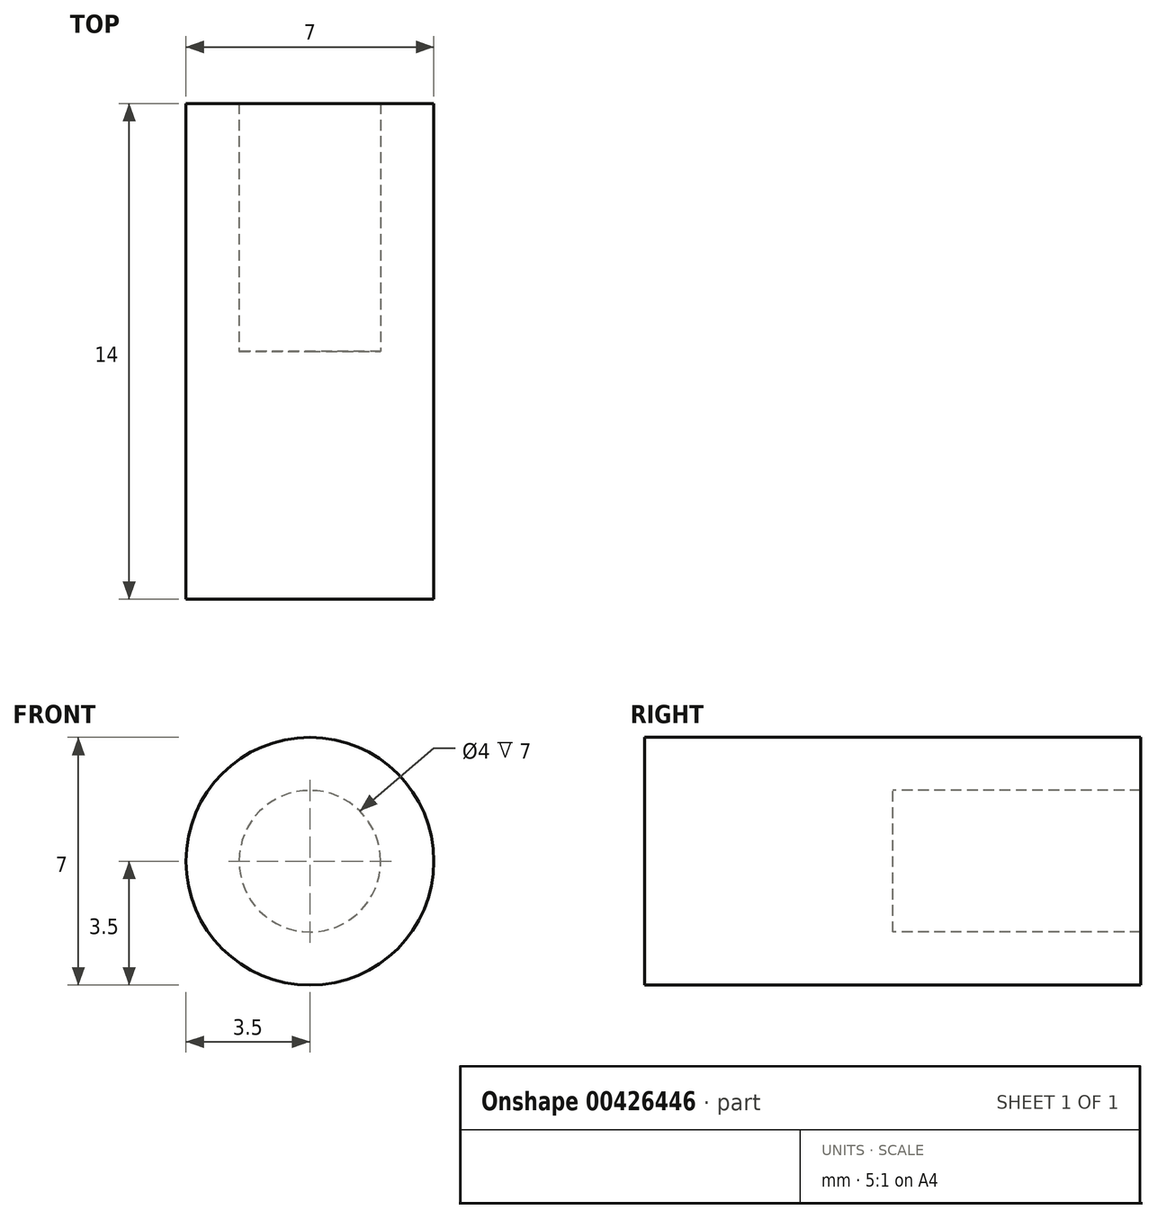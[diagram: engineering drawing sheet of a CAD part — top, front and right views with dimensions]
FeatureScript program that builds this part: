
annotation { "Feature Type Name" : "Feature", "Feature Type Description" : "" }
export const myFeature = defineFeature(function(context is Context, id is Id, definition is map)
    precondition{}
    {
        {
            var Q0;
            Q0=qCreatedBy(makeId("Right.planeOp"),FACE);
            var sketch = newSketch(context, id + "F0", { "sketchPlane" : qUnion([Q0])});
            skLineSegment(sketch, "E0.bottom", {"start": v(-7, 3.5) * mm, "end": v(7, 3.5) * mm});
            skLineSegment(sketch, "E0.left", {"start": v(-7, 3.5) * mm, "end": v(-7, 0) * mm});
            skLineSegment(sketch, "E0.right", {"start": v(7, 3.5) * mm, "end": v(7, 0) * mm});
            skPoint(sketch, "E0.middle", {"position": v(0, 0) * mm});
            skLineSegment(sketch, "E1", {"start": v(-7, 0) * mm, "end": v(0, 0) * mm});
            skLineSegment(sketch, "E2", {"start": v(0, 2) * mm, "end": v(7, 2) * mm});
            skLineSegment(sketch, "E3", {"start": v(0, 0) * mm, "end": v(0, 2) * mm});
            skPoint(sketch, "E4.orphan", {"position": v(-7, 2) * mm});
            skPoint(sketch, "E5.orphan", {"position": v(7, 0) * mm});
            skPoint(sketch, "E6.orphan", {"position": v(7, -3.5) * mm});
            skPoint(sketch, "E7.orphan", {"position": v(-7, -3.5) * mm});
            skLineSegment(sketch, "E8", {"start": v(-21.07, 0) * mm, "end": v(21.6, 0) * mm, "construction": true});
            skSolve(sketch);
        }
        {
            var Q0;
            Q0 = qSketchRegion(id + "F0", true);
            var Q1;
            Q1=sQuery(id+"F0.wireOp",EDGE,"E8");
            revolve(context, id + "F1", {"entities" : qUnion([Q0]), "axis" : qUnion([Q1]), "revolveType" : RevolveType.FULL});
        }
    });
